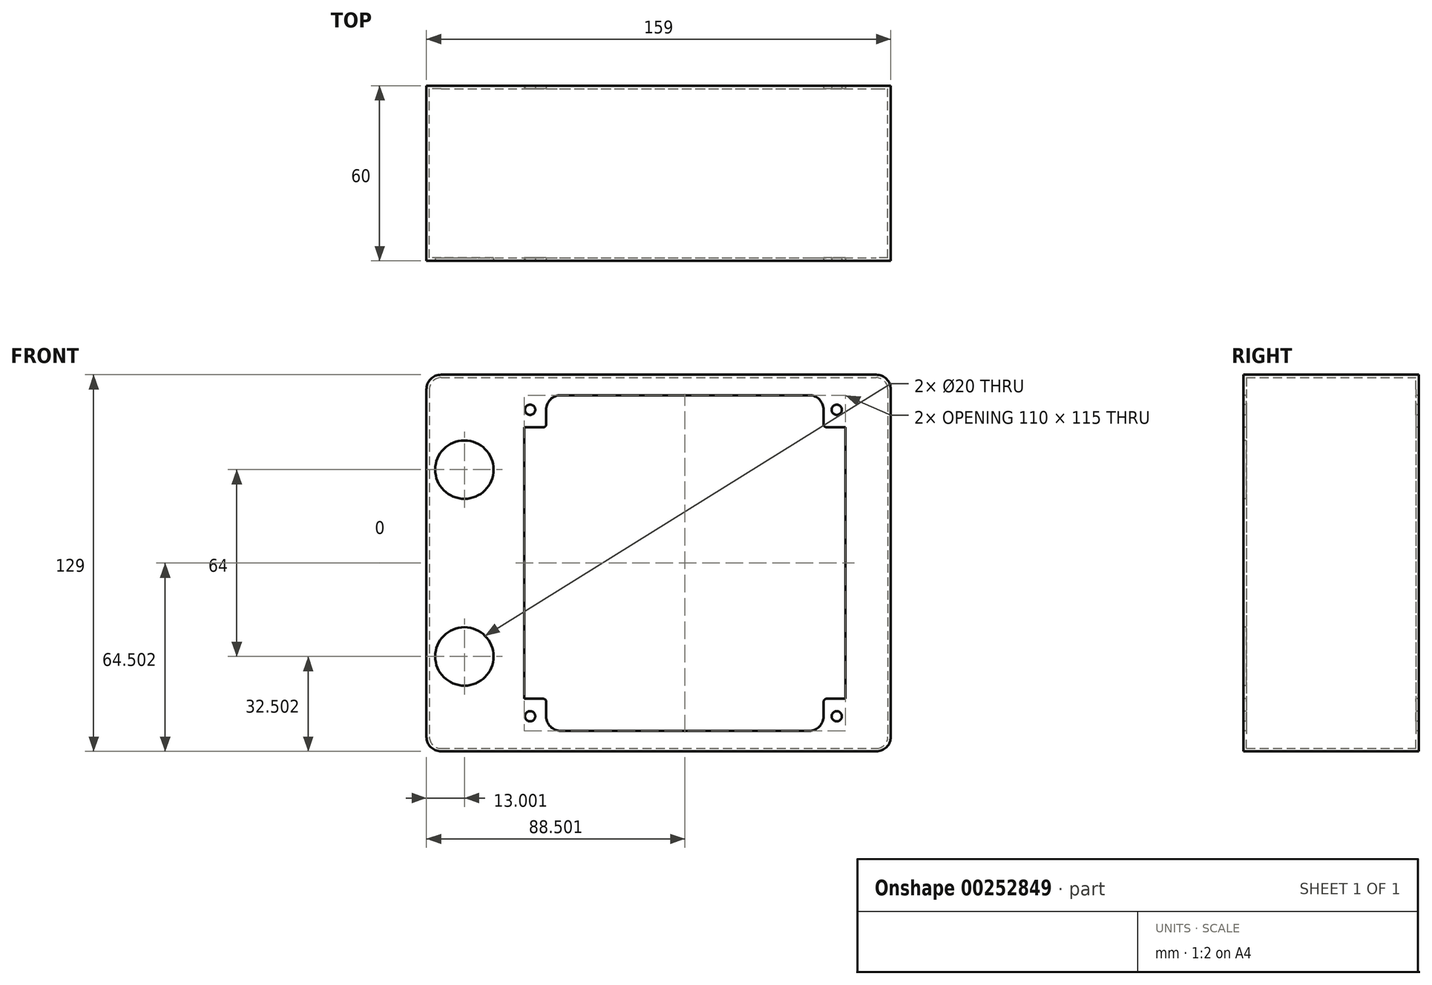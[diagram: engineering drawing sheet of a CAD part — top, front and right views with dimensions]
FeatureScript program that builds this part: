
annotation { "Feature Type Name" : "Feature", "Feature Type Description" : "" }
export const myFeature = defineFeature(function(context is Context, id is Id, definition is map)
    precondition{}
    {
        {
            var Q0;
            Q0=qCreatedBy(makeId("Front.planeOp"),FACE);
            var sketch = newSketch(context, id + "F0", { "sketchPlane" : qUnion([Q0])});
            skLineSegment(sketch, "E0.bottom", {"start": v(-74.39, 61.74) * mm, "end": v(84.61, 61.74) * mm});
            skLineSegment(sketch, "E0.top", {"start": v(-74.39, -67.26) * mm, "end": v(84.61, -67.26) * mm});
            skLineSegment(sketch, "E0.left", {"start": v(-74.39, 61.74) * mm, "end": v(-74.39, -67.26) * mm});
            skLineSegment(sketch, "E0.right", {"start": v(84.61, 61.74) * mm, "end": v(84.61, -67.26) * mm});
            skSolve(sketch);
        }
        {
            var Q0;
            Q0=makeQuery(id+"F0.imprint","IMPRINT",FACE,{"disambiguationData":[TD([[makeQuery(id+"F0.imprint","IMPRINT",EDGE,{"derivedFrom":sQuery(id+"F0.wireOp",EDGE,"E0.bottom")}),-1.0]])]});
            extrude(context, id + "F1", {"entities" : qUnion([Q0]), "depth" : 60 * mm});
        }
        {
            var Q0;
            Q0=makeQuery(id+"F1.opExtrude","SWEPT_EDGE",EDGE,{"disambiguationData":[OSD([sQuery(id+"F0.wireOp",EDGE,"E0.top"),sQuery(id+"F0.wireOp",EDGE,"E0.right")])]});
            var Q1;
            Q1=makeQuery(id+"F1.opExtrude","SWEPT_EDGE",EDGE,{"disambiguationData":[OSD([sQuery(id+"F0.wireOp",EDGE,"E0.bottom"),sQuery(id+"F0.wireOp",EDGE,"E0.right")])]});
            var Q2;
            Q2=makeQuery(id+"F1.opExtrude","SWEPT_EDGE",EDGE,{"disambiguationData":[OSD([sQuery(id+"F0.wireOp",EDGE,"E0.bottom"),sQuery(id+"F0.wireOp",EDGE,"E0.left")])]});
            var Q3;
            Q3=makeQuery(id+"F1.opExtrude","SWEPT_EDGE",EDGE,{"disambiguationData":[OSD([sQuery(id+"F0.wireOp",EDGE,"E0.top"),sQuery(id+"F0.wireOp",EDGE,"E0.left")])]});
            fillet(context, id + "F2", {"entities" : qUnion([Q0, Q1, Q2, Q3]), "radius" : 5 * mm, "tangentPropagation" : true, "allowEdgeOverflow" : false});
        }
        {
            var Q0;
            Q0=makeQuery(id+"F1.opExtrude","CAP_FACE",FACE,{"disambiguationData":[OSD([sQuery(id+"F0.wireOp",EDGE,"E0.bottom"),sQuery(id+"F0.wireOp",EDGE,"E0.top"),sQuery(id+"F0.wireOp",EDGE,"E0.left"),sQuery(id+"F0.wireOp",EDGE,"E0.right")])],"isStart":false});
            var sketch = newSketch(context, id + "F3", { "sketchPlane" : qUnion([Q0])});
            skLineSegment(sketch, "E1.bottom", {"start": v(69.11, 43.74) * mm, "end": v(-40.89, 43.74) * mm});
            skLineSegment(sketch, "E1.top", {"start": v(69.11, -49.26) * mm, "end": v(-40.89, -49.26) * mm});
            skLineSegment(sketch, "E1.left", {"start": v(69.11, 43.74) * mm, "end": v(69.11, -49.26) * mm});
            skLineSegment(sketch, "E1.right", {"start": v(-40.89, 43.74) * mm, "end": v(-40.89, -49.26) * mm});
            skLineSegment(sketch, "E2.bottom", {"start": v(-33.39, 54.74) * mm, "end": v(61.61, 54.74) * mm});
            skLineSegment(sketch, "E2.top", {"start": v(-33.39, -60.26) * mm, "end": v(61.61, -60.26) * mm});
            skLineSegment(sketch, "E2.left", {"start": v(-33.39, 54.74) * mm, "end": v(-33.39, -60.26) * mm});
            skLineSegment(sketch, "E2.right", {"start": v(61.61, 54.74) * mm, "end": v(61.61, -60.26) * mm});
            skSolve(sketch);
        }
        {
            var Q0;
            {var subQ0=sQuery(id+"F3.wireOp",EDGE,"E1.right");Q0=makeQuery(id+"F3.imprint","IMPRINT",FACE,{"disambiguationData":[TD([[makeQuery(id+"F3.imprint","IMPRINT",EDGE,{"derivedFrom":subQ0}),1.0]])]});}
            var Q1;
            {var subQ0=sQuery(id+"F3.wireOp",EDGE,"E2.right");var subQ1=sQuery(id+"F3.wireOp",EDGE,"E1.bottom");var subQ2=makeQuery(id+"F3.imprint","INTERSECT",VERTEX,{"derivedFrom":[subQ1,subQ0]});Q1=makeQuery(id+"F3.imprint","IMPRINT",FACE,{"disambiguationData":[TD([[makeQuery(id+"F3.imprint","IMPRINT",EDGE,{"disambiguationData":[TD([[subQ2,-1.0]])],"derivedFrom":subQ1}),1.0]])]});}
            var Q2;
            {var subQ5=sQuery(id+"F3.wireOp",EDGE,"E2.bottom");Q2=makeQuery(id+"F3.imprint","IMPRINT",FACE,{"disambiguationData":[TD([[makeQuery(id+"F3.imprint","IMPRINT",EDGE,{"derivedFrom":subQ5}),-1.0]])]});}
            var Q3;
            {var subQ0=sQuery(id+"F3.wireOp",EDGE,"E1.left");Q3=makeQuery(id+"F3.imprint","IMPRINT",FACE,{"disambiguationData":[TD([[makeQuery(id+"F3.imprint","IMPRINT",EDGE,{"derivedFrom":subQ0}),-1.0]])]});}
            var Q4;
            {var subQ5=sQuery(id+"F3.wireOp",EDGE,"E2.top");Q4=makeQuery(id+"F3.imprint","IMPRINT",FACE,{"disambiguationData":[TD([[makeQuery(id+"F3.imprint","IMPRINT",EDGE,{"derivedFrom":subQ5}),1.0]])]});}
            extrude(context, id + "F4", {"entities" : qUnion([Q0, Q1, Q2, Q3, Q4]), "operationType" : NewBodyOperationType.REMOVE, "oppositeDirection" : true, "depth" : 97 * mm});
        }
        {
            var Q0;
            Q0=makeQuery(id+"F4.boolean.opBoolean","COPY",EDGE,{"derivedFrom":makeQuery(id+"F4.opExtrude","SWEPT_EDGE",EDGE,{"disambiguationData":[OSD([sQuery(id+"F3.wireOp",EDGE,"E2.bottom"),sQuery(id+"F3.wireOp",EDGE,"E2.left")])]})});
            var Q1;
            Q1=makeQuery(id+"F4.boolean.opBoolean","COPY",EDGE,{"derivedFrom":makeQuery(id+"F4.opExtrude","SWEPT_EDGE",EDGE,{"disambiguationData":[OSD([sQuery(id+"F3.wireOp",EDGE,"E2.bottom"),sQuery(id+"F3.wireOp",EDGE,"E2.right")])]})});
            var Q2;
            Q2=makeQuery(id+"F4.boolean.opBoolean","COPY",EDGE,{"derivedFrom":makeQuery(id+"F4.opExtrude","SWEPT_EDGE",EDGE,{"disambiguationData":[OSD([sQuery(id+"F3.wireOp",EDGE,"E2.top"),sQuery(id+"F3.wireOp",EDGE,"E2.right")])]})});
            var Q3;
            Q3=makeQuery(id+"F4.boolean.opBoolean","COPY",EDGE,{"derivedFrom":makeQuery(id+"F4.opExtrude","SWEPT_EDGE",EDGE,{"disambiguationData":[OSD([sQuery(id+"F3.wireOp",EDGE,"E2.top"),sQuery(id+"F3.wireOp",EDGE,"E2.left")])]})});
            fillet(context, id + "F5", {"entities" : qUnion([Q0, Q1, Q2, Q3]), "radius" : 5 * mm, "tangentPropagation" : true, "allowEdgeOverflow" : false});
        }
        {
            var Q0;
            Q0=makeQuery(id+"F4.boolean.opBoolean","COPY",EDGE,{"derivedFrom":makeQuery(id+"F4.opExtrude","SWEPT_EDGE",EDGE,{"disambiguationData":[OSD([sQuery(id+"F3.wireOp",EDGE,"E1.bottom"),sQuery(id+"F3.wireOp",EDGE,"E2.left")])]})});
            var Q1;
            Q1=makeQuery(id+"F4.boolean.opBoolean","COPY",EDGE,{"derivedFrom":makeQuery(id+"F4.opExtrude","SWEPT_EDGE",EDGE,{"disambiguationData":[OSD([sQuery(id+"F3.wireOp",EDGE,"E1.bottom"),sQuery(id+"F3.wireOp",EDGE,"E2.right")])]})});
            var Q2;
            Q2=makeQuery(id+"F4.boolean.opBoolean","COPY",EDGE,{"derivedFrom":makeQuery(id+"F4.opExtrude","SWEPT_EDGE",EDGE,{"disambiguationData":[OSD([sQuery(id+"F3.wireOp",EDGE,"E1.top"),sQuery(id+"F3.wireOp",EDGE,"E2.right")])]})});
            var Q3;
            Q3=makeQuery(id+"F4.boolean.opBoolean","COPY",EDGE,{"derivedFrom":makeQuery(id+"F4.opExtrude","SWEPT_EDGE",EDGE,{"disambiguationData":[OSD([sQuery(id+"F3.wireOp",EDGE,"E1.top"),sQuery(id+"F3.wireOp",EDGE,"E2.left")])]})});
            fillet(context, id + "F6", {"entities" : qUnion([Q0, Q1, Q2, Q3]), "radius" : 1 * mm, "tangentPropagation" : true, "allowEdgeOverflow" : false});
        }
        {
            var Q0;
            {var subQ0=sQuery(id+"F3.wireOp",EDGE,"E1.bottom");Q0=makeQuery(id+"F4.boolean.opBoolean","COPY",FACE,{"derivedFrom":makeQuery(id+"F4.opExtrude","SWEPT_FACE",FACE,{"disambiguationData":[OSD([subQ0]),TDD([makeQuery(id+"F3.imprint","IMPRINT",EDGE,{"disambiguationData":[TD([[makeQuery(id+"F3.imprint","INTERSECT",VERTEX,{"derivedFrom":[subQ0,sQuery(id+"F3.wireOp",EDGE,"E1.right")]}),1.0]])],"derivedFrom":subQ0})])]})});}
            var Q1;
            {var subQ0=sQuery(id+"F3.wireOp",EDGE,"E2.left");Q1=makeQuery(id+"F4.boolean.opBoolean","COPY",FACE,{"derivedFrom":makeQuery(id+"F4.opExtrude","SWEPT_FACE",FACE,{"disambiguationData":[OSD([subQ0]),TDD([makeQuery(id+"F3.imprint","IMPRINT",EDGE,{"disambiguationData":[TD([[makeQuery(id+"F3.imprint","INTERSECT",VERTEX,{"derivedFrom":[sQuery(id+"F3.wireOp",EDGE,"E2.bottom"),subQ0]}),-1.0]])],"derivedFrom":subQ0})])]})});}
            var Q2;
            Q2=makeQuery(id+"F5.opFillet","BLEND_FACE",FACE,{"disambiguationData":[OSD([sQuery(id+"F3.wireOp",EDGE,"E2.bottom"),sQuery(id+"F3.wireOp",EDGE,"E2.left")])]});
            var Q3;
            Q3=makeQuery(id+"F4.boolean.opBoolean","COPY",FACE,{"derivedFrom":makeQuery(id+"F4.opExtrude","SWEPT_FACE",FACE,{"disambiguationData":[OSD([sQuery(id+"F3.wireOp",EDGE,"E2.bottom")])]})});
            var Q4;
            Q4=makeQuery(id+"F5.opFillet","BLEND_FACE",FACE,{"disambiguationData":[OSD([sQuery(id+"F3.wireOp",EDGE,"E2.bottom"),sQuery(id+"F3.wireOp",EDGE,"E2.right")])]});
            var Q5;
            {var subQ0=sQuery(id+"F3.wireOp",EDGE,"E2.right");Q5=makeQuery(id+"F4.boolean.opBoolean","COPY",FACE,{"derivedFrom":makeQuery(id+"F4.opExtrude","SWEPT_FACE",FACE,{"disambiguationData":[OSD([subQ0]),TDD([makeQuery(id+"F3.imprint","IMPRINT",EDGE,{"disambiguationData":[TD([[makeQuery(id+"F3.imprint","INTERSECT",VERTEX,{"derivedFrom":[sQuery(id+"F3.wireOp",EDGE,"E2.bottom"),subQ0]}),-1.0]])],"derivedFrom":subQ0})])]})});}
            var Q6;
            {var subQ0=sQuery(id+"F3.wireOp",EDGE,"E1.bottom");Q6=makeQuery(id+"F4.boolean.opBoolean","COPY",FACE,{"derivedFrom":makeQuery(id+"F4.opExtrude","SWEPT_FACE",FACE,{"disambiguationData":[OSD([subQ0]),TDD([makeQuery(id+"F3.imprint","IMPRINT",EDGE,{"disambiguationData":[TD([[makeQuery(id+"F3.imprint","INTERSECT",VERTEX,{"derivedFrom":[subQ0,sQuery(id+"F3.wireOp",EDGE,"E1.left")]}),-1.0]])],"derivedFrom":subQ0})])]})});}
            var Q7;
            Q7=makeQuery(id+"F4.boolean.opBoolean","COPY",FACE,{"derivedFrom":makeQuery(id+"F4.opExtrude","SWEPT_FACE",FACE,{"disambiguationData":[OSD([sQuery(id+"F3.wireOp",EDGE,"E1.left")])]})});
            var Q8;
            {var subQ0=sQuery(id+"F3.wireOp",EDGE,"E1.top");Q8=makeQuery(id+"F4.boolean.opBoolean","COPY",FACE,{"derivedFrom":makeQuery(id+"F4.opExtrude","SWEPT_FACE",FACE,{"disambiguationData":[OSD([subQ0]),TDD([makeQuery(id+"F3.imprint","IMPRINT",EDGE,{"disambiguationData":[TD([[makeQuery(id+"F3.imprint","INTERSECT",VERTEX,{"derivedFrom":[subQ0,sQuery(id+"F3.wireOp",EDGE,"E1.left")]}),-1.0]])],"derivedFrom":subQ0})])]})});}
            var Q9;
            {var subQ0=sQuery(id+"F3.wireOp",EDGE,"E2.right");Q9=makeQuery(id+"F4.boolean.opBoolean","COPY",FACE,{"derivedFrom":makeQuery(id+"F4.opExtrude","SWEPT_FACE",FACE,{"disambiguationData":[OSD([subQ0]),TDD([makeQuery(id+"F3.imprint","IMPRINT",EDGE,{"disambiguationData":[TD([[makeQuery(id+"F3.imprint","INTERSECT",VERTEX,{"derivedFrom":[sQuery(id+"F3.wireOp",EDGE,"E2.top"),subQ0]}),1.0]])],"derivedFrom":subQ0})])]})});}
            var Q10;
            Q10=makeQuery(id+"F5.opFillet","BLEND_FACE",FACE,{"disambiguationData":[OSD([sQuery(id+"F3.wireOp",EDGE,"E2.top"),sQuery(id+"F3.wireOp",EDGE,"E2.right")])]});
            var Q11;
            Q11=makeQuery(id+"F4.boolean.opBoolean","COPY",FACE,{"derivedFrom":makeQuery(id+"F4.opExtrude","SWEPT_FACE",FACE,{"disambiguationData":[OSD([sQuery(id+"F3.wireOp",EDGE,"E2.top")])]})});
            var Q12;
            Q12=makeQuery(id+"F5.opFillet","BLEND_FACE",FACE,{"disambiguationData":[OSD([sQuery(id+"F3.wireOp",EDGE,"E2.top"),sQuery(id+"F3.wireOp",EDGE,"E2.left")])]});
            var Q13;
            {var subQ0=sQuery(id+"F3.wireOp",EDGE,"E2.left");Q13=makeQuery(id+"F4.boolean.opBoolean","COPY",FACE,{"derivedFrom":makeQuery(id+"F4.opExtrude","SWEPT_FACE",FACE,{"disambiguationData":[OSD([subQ0]),TDD([makeQuery(id+"F3.imprint","IMPRINT",EDGE,{"disambiguationData":[TD([[makeQuery(id+"F3.imprint","INTERSECT",VERTEX,{"derivedFrom":[sQuery(id+"F3.wireOp",EDGE,"E2.top"),subQ0]}),1.0]])],"derivedFrom":subQ0})])]})});}
            var Q14;
            {var subQ0=sQuery(id+"F3.wireOp",EDGE,"E1.top");Q14=makeQuery(id+"F4.boolean.opBoolean","COPY",FACE,{"derivedFrom":makeQuery(id+"F4.opExtrude","SWEPT_FACE",FACE,{"disambiguationData":[OSD([subQ0]),TDD([makeQuery(id+"F3.imprint","IMPRINT",EDGE,{"disambiguationData":[TD([[makeQuery(id+"F3.imprint","INTERSECT",VERTEX,{"derivedFrom":[subQ0,sQuery(id+"F3.wireOp",EDGE,"E1.right")]}),1.0]])],"derivedFrom":subQ0})])]})});}
            var Q15;
            Q15=makeQuery(id+"F4.boolean.opBoolean","COPY",FACE,{"derivedFrom":makeQuery(id+"F4.opExtrude","SWEPT_FACE",FACE,{"disambiguationData":[OSD([sQuery(id+"F3.wireOp",EDGE,"E1.right")])]})});
            var Q16;
            Q16=makeQuery(id+"F6.opFillet","BLEND_FACE",FACE,{"disambiguationData":[OSD([sQuery(id+"F3.wireOp",EDGE,"E1.bottom"),sQuery(id+"F3.wireOp",EDGE,"E2.left")])]});
            var Q17;
            Q17=makeQuery(id+"F6.opFillet","BLEND_FACE",FACE,{"disambiguationData":[OSD([sQuery(id+"F3.wireOp",EDGE,"E1.bottom"),sQuery(id+"F3.wireOp",EDGE,"E2.right")])]});
            var Q18;
            Q18=makeQuery(id+"F6.opFillet","BLEND_FACE",FACE,{"disambiguationData":[OSD([sQuery(id+"F3.wireOp",EDGE,"E1.top"),sQuery(id+"F3.wireOp",EDGE,"E2.right")])]});
            var Q19;
            Q19=makeQuery(id+"F6.opFillet","BLEND_FACE",FACE,{"disambiguationData":[OSD([sQuery(id+"F3.wireOp",EDGE,"E1.top"),sQuery(id+"F3.wireOp",EDGE,"E2.left")])]});
            shell(context, id + "F7", {"entities" : qUnion([Q0, Q1, Q2, Q3, Q4, Q5, Q6, Q7, Q8, Q9, Q10, Q11, Q12, Q13, Q14, Q15, Q16, Q17, Q18, Q19]), "thickness" : 1 * mm});
        }
        {
            var Q0;
            Q0=makeQuery(id+"F1.opExtrude","CAP_FACE",FACE,{"disambiguationData":[OSD([sQuery(id+"F0.wireOp",EDGE,"E0.bottom"),sQuery(id+"F0.wireOp",EDGE,"E0.top"),sQuery(id+"F0.wireOp",EDGE,"E0.left"),sQuery(id+"F0.wireOp",EDGE,"E0.right")])],"isStart":false});
            var sketch = newSketch(context, id + "F8", { "sketchPlane" : qUnion([Q0])});
            skPoint(sketch, "E3", {"position": v(-38.89, 49.74) * mm});
            skPoint(sketch, "E4", {"position": v(66.11, 49.74) * mm});
            skPoint(sketch, "E5", {"position": v(66.11, -55.26) * mm});
            skPoint(sketch, "E6", {"position": v(-38.89, -55.26) * mm});
            skSolve(sketch);
        }
        {
            var Q0;
            Q0=sQuery(id+"F8.wireOp",VERTEX,"E3");
            var Q1;
            Q1=sQuery(id+"F8.wireOp",VERTEX,"E4");
            var Q2;
            Q2=sQuery(id+"F8.wireOp",VERTEX,"E5");
            var Q3;
            Q3=sQuery(id+"F8.wireOp",VERTEX,"E6");
            var Q4;
            Q4=makeQuery(id+"F1.opExtrude","SWEPT_BODY",BODY,{"disambiguationData":[OSD([sQuery(id+"F0.wireOp",EDGE,"E0.bottom"),sQuery(id+"F0.wireOp",EDGE,"E0.top"),sQuery(id+"F0.wireOp",EDGE,"E0.left"),sQuery(id+"F0.wireOp",EDGE,"E0.right")])]});
            hole(context, id + "F9", {"style" : HoleStyle.SIMPLE, "endStyle" : HoleEndStyle.THROUGH, "holeDiameter" : 3.5 * mm, "tappedDepth" : 12 * mm, "tapClearance" : 3, "locations" : qUnion([Q0, Q1, Q2, Q3]), "scope" : qUnion([Q4])});
        }
        {
            var Q0;
            Q0=makeQuery(id+"F1.opExtrude","CAP_FACE",FACE,{"disambiguationData":[OSD([sQuery(id+"F0.wireOp",EDGE,"E0.bottom"),sQuery(id+"F0.wireOp",EDGE,"E0.top"),sQuery(id+"F0.wireOp",EDGE,"E0.left"),sQuery(id+"F0.wireOp",EDGE,"E0.right")])],"isStart":false});
            var sketch = newSketch(context, id + "F10", { "sketchPlane" : qUnion([Q0])});
            skCircle(sketch, "E7", {"center": v(-61.39, 29.24) * mm, "radius": 10 * mm});
            skCircle(sketch, "E8", {"center": v(-61.39, -34.76) * mm, "radius": 10 * mm});
            skSolve(sketch);
        }
        {
            var Q0;
            Q0=makeQuery(id+"F10.imprint","IMPRINT",FACE,{"disambiguationData":[TD([[makeQuery(id+"F10.imprint","IMPRINT",EDGE,{"derivedFrom":sQuery(id+"F10.wireOp",EDGE,"E7")}),1.0]])]});
            var Q1;
            Q1=makeQuery(id+"F10.imprint","IMPRINT",FACE,{"disambiguationData":[TD([[makeQuery(id+"F10.imprint","IMPRINT",EDGE,{"derivedFrom":sQuery(id+"F10.wireOp",EDGE,"E8")}),1.0]])]});
            var Q2;
            Q2=sQuery(id+"F10.wireOp",EDGE,"E7");
            var Q3;
            Q3=sQuery(id+"F10.wireOp",EDGE,"E8");
            extrude(context, id + "F11", {"entities" : qUnion([Q0, Q1]), "operationType" : NewBodyOperationType.REMOVE, "surfaceEntities" : qUnion([Q2, Q3]), "oppositeDirection" : true, "depth" : 10 * mm});
        }
    });
